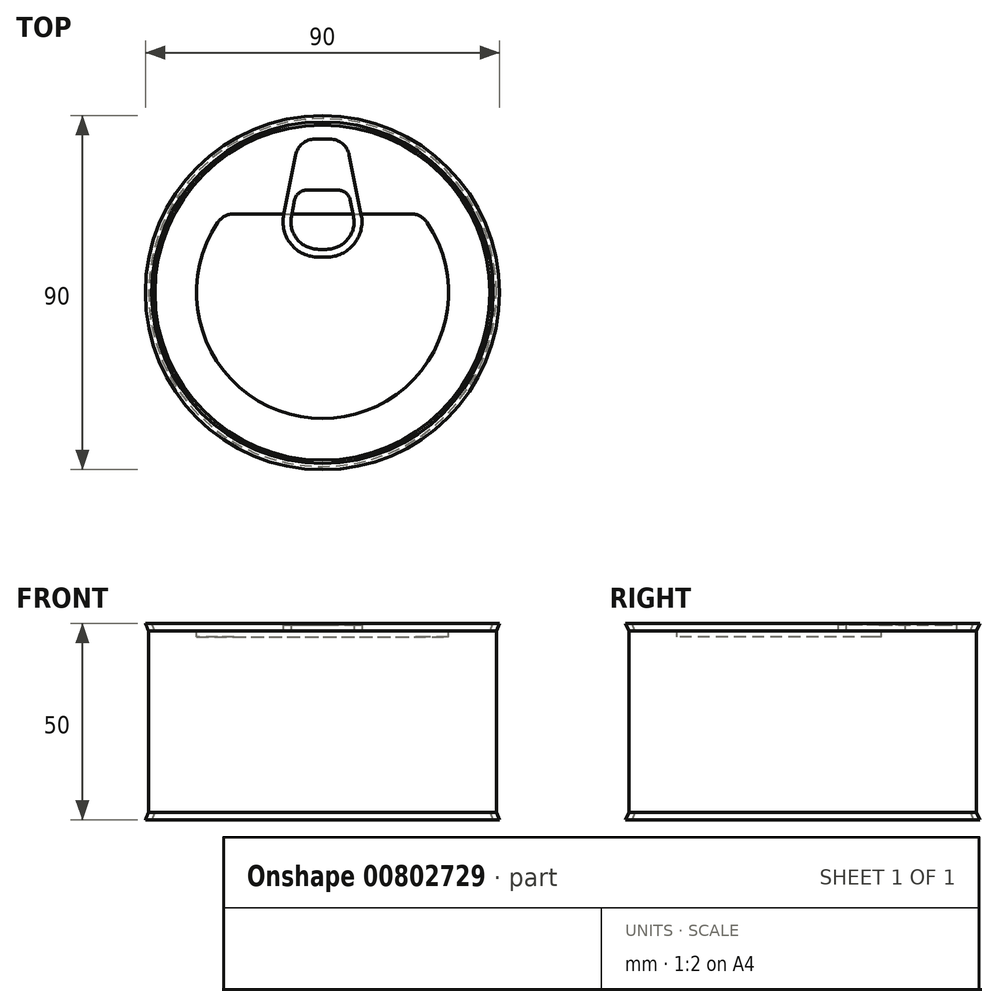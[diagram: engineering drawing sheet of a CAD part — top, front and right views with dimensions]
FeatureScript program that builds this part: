
annotation { "Feature Type Name" : "Feature", "Feature Type Description" : "" }
export const myFeature = defineFeature(function(context is Context, id is Id, definition is map)
    precondition{}
    {
        {
            var Q0;
            Q0=qCreatedBy(makeId("Right.planeOp"),FACE);
            var sketch = newSketch(context, id + "F0", { "sketchPlane" : qUnion([Q0])});
            skLineSegment(sketch, "E0", {"start": v(0, 2) * mm, "end": v(0, 48) * mm});
            skLineSegment(sketch, "E1", {"start": v(0, 48) * mm, "end": v(42.67, 48) * mm});
            skLineSegment(sketch, "E2", {"start": v(42.57, 48) * mm, "end": v(43.38, 50) * mm});
            skLineSegment(sketch, "E3", {"start": v(43.38, 50) * mm, "end": v(45, 50) * mm});
            skLineSegment(sketch, "E4", {"start": v(45, 50) * mm, "end": v(44.2, 48) * mm});
            skLineSegment(sketch, "E5", {"start": v(44.2, 48) * mm, "end": v(44.2, 2) * mm});
            skLineSegment(sketch, "E6", {"start": v(44.2, 2) * mm, "end": v(45, 0) * mm});
            skLineSegment(sketch, "E7", {"start": v(45, 0) * mm, "end": v(43.38, 0) * mm});
            skLineSegment(sketch, "E8", {"start": v(43.38, 0) * mm, "end": v(42.57, 2) * mm});
            skLineSegment(sketch, "E9", {"start": v(42.57, 2) * mm, "end": v(0, 2) * mm});
            skPoint(sketch, "E10", {"position": v(44.2, 0) * mm});
            skSolve(sketch);
        }
        {
            var Q0;
            Q0=makeQuery(id+"F0.imprint","IMPRINT",FACE,{"disambiguationData":[TD([[makeQuery(id+"F0.imprint","IMPRINT",EDGE,{"derivedFrom":sQuery(id+"F0.wireOp",EDGE,"E0")}),-1.0]])]});
            var Q1;
            Q1=sQuery(id+"F0.wireOp",EDGE,"E0");
            revolve(context, id + "F1", {"surfaceOperationType" : NewSurfaceOperationType.NEW, "entities" : qUnion([Q0]), "axis" : qUnion([Q1]), "revolveType" : RevolveType.FULL});
        }
        {
            var Q0;
            Q0=makeQuery(id+"F1.opRevolve","SWEPT_FACE",FACE,{"disambiguationData":[OSD([sQuery(id+"F0.wireOp",EDGE,"E1")])]});
            var sketch = newSketch(context, id + "F2", { "sketchPlane" : qUnion([Q0])});
            skArc(sketch, "E11", {"start": v(-26.6, 17.78) * mm, "mid": v(0, -32) * mm, "end": v(26.6, 17.78) * mm});
            skLineSegment(sketch, "E12", {"start": v(-22.45, 20) * mm, "end": v(22.45, 20) * mm});
            skPoint(sketch, "E13.visualSharp", {"position": v(-24.98, 20) * mm});
            skArc(sketch, "E13.filletArc", {"start": v(-22.45, 20) * mm, "mid": v(-24.8, 19.4) * mm, "end": v(-26.6, 17.78) * mm});
            skPoint(sketch, "E14.visualSharp", {"position": v(24.98, 20) * mm});
            skArc(sketch, "E14.filletArc", {"start": v(26.6, 17.78) * mm, "mid": v(24.8, 19.4) * mm, "end": v(22.45, 20) * mm});
            skSolve(sketch);
        }
        {
            var Q0;
            Q0=makeQuery(id+"F2.imprint","IMPRINT",FACE,{"disambiguationData":[TD([[makeQuery(id+"F2.imprint","IMPRINT",EDGE,{"derivedFrom":sQuery(id+"F2.wireOp",EDGE,"E11")}),1.0]])]});
            extrude(context, id + "F3", {"entities" : qUnion([Q0]), "operationType" : NewBodyOperationType.REMOVE, "oppositeDirection" : true, "depth" : 1.5 * mm, "offsetDistance" : 25 * mm});
        }
        {
            var Q0;
            Q0=makeQuery(id+"F1.opRevolve","SWEPT_FACE",FACE,{"disambiguationData":[OSD([sQuery(id+"F0.wireOp",EDGE,"E1")])]});
            var sketch = newSketch(context, id + "F4", { "sketchPlane" : qUnion([Q0])});
            skLineSegment(sketch, "E15", {"start": v(-1.9, 39) * mm, "end": v(1.9, 39) * mm});
            skLineSegment(sketch, "E16", {"start": v(6.8, 34.98) * mm, "end": v(9.85, 19.77) * mm});
            skLineSegment(sketch, "E17", {"start": v(1.02, 9) * mm, "end": v(-1.02, 9) * mm});
            skLineSegment(sketch, "E18", {"start": v(-9.85, 19.77) * mm, "end": v(-6.8, 34.98) * mm});
            skPoint(sketch, "E19.visualSharp", {"position": v(-12, 9) * mm});
            skArc(sketch, "E19.filletArc", {"start": v(-9.85, 19.77) * mm, "mid": v(-7.98, 12.3) * mm, "end": v(-1.02, 9) * mm});
            skPoint(sketch, "E20.visualSharp", {"position": v(12, 9) * mm});
            skArc(sketch, "E20.filletArc", {"start": v(1.02, 9) * mm, "mid": v(7.98, 12.3) * mm, "end": v(9.85, 19.77) * mm});
            skPoint(sketch, "E21.visualSharp", {"position": v(-6, 39) * mm});
            skArc(sketch, "E21.filletArc", {"start": v(-1.9, 39) * mm, "mid": v(-5.07, 37.87) * mm, "end": v(-6.8, 34.98) * mm});
            skPoint(sketch, "E22.visualSharp", {"position": v(6, 39) * mm});
            skArc(sketch, "E22.filletArc", {"start": v(6.8, 34.98) * mm, "mid": v(5.07, 37.87) * mm, "end": v(1.9, 39) * mm});
            skPoint(sketch, "E23", {"position": v(0, 39) * mm});
            skPoint(sketch, "E24", {"position": v(0, 9) * mm});
            skArc(sketch, "E25.0", {"start": v(1.02, 11) * mm, "mid": v(6.44, 13.56) * mm, "end": v(7.89, 19.37) * mm});
            skLineSegment(sketch, "E25.1", {"start": v(1.02, 11) * mm, "end": v(-1.02, 11) * mm});
            skArc(sketch, "E25.2", {"start": v(-7.89, 19.37) * mm, "mid": v(-6.44, 13.56) * mm, "end": v(-1.02, 11) * mm});
            skLineSegment(sketch, "E26", {"start": v(-7.89, 19.37) * mm, "end": v(-7.04, 23.59) * mm});
            skLineSegment(sketch, "E27", {"start": v(-4.1, 26) * mm, "end": v(4.1, 26) * mm});
            skLineSegment(sketch, "E28", {"start": v(7.89, 19.37) * mm, "end": v(7.04, 23.59) * mm});
            skPoint(sketch, "E29.visualSharp", {"position": v(-6.56, 26) * mm});
            skArc(sketch, "E29.filletArc", {"start": v(-4.1, 26) * mm, "mid": v(-6, 25.32) * mm, "end": v(-7.04, 23.59) * mm});
            skPoint(sketch, "E30.visualSharp", {"position": v(6.56, 26) * mm});
            skArc(sketch, "E30.filletArc", {"start": v(7.04, 23.59) * mm, "mid": v(6, 25.32) * mm, "end": v(4.1, 26) * mm});
            skSolve(sketch);
        }
        {
            var Q0;
            {var subQ0=sQuery(id+"F4.wireOp",EDGE,"E15");Q0=makeQuery(id+"F4.imprint","IMPRINT",FACE,{"disambiguationData":[TD([[makeQuery(id+"F4.imprint","IMPRINT",EDGE,{"derivedFrom":subQ0}),-1.0]])]});}
            var Q1;
            {var subQ1=sQuery(id+"F4.wireOp",EDGE,"E16");Q1=makeQuery(id+"F4.imprint","IMPRINT",FACE,{"disambiguationData":[TD([[makeQuery(id+"F4.imprint","IMPRINT",EDGE,{"derivedFrom":subQ1}),-1.0]])]});}
            extrude(context, id + "F5", {"entities" : qUnion([Q0, Q1]), "operationType" : NewBodyOperationType.ADD, "depth" : 1.5 * mm, "offsetDistance" : 25 * mm});
        }
    });
